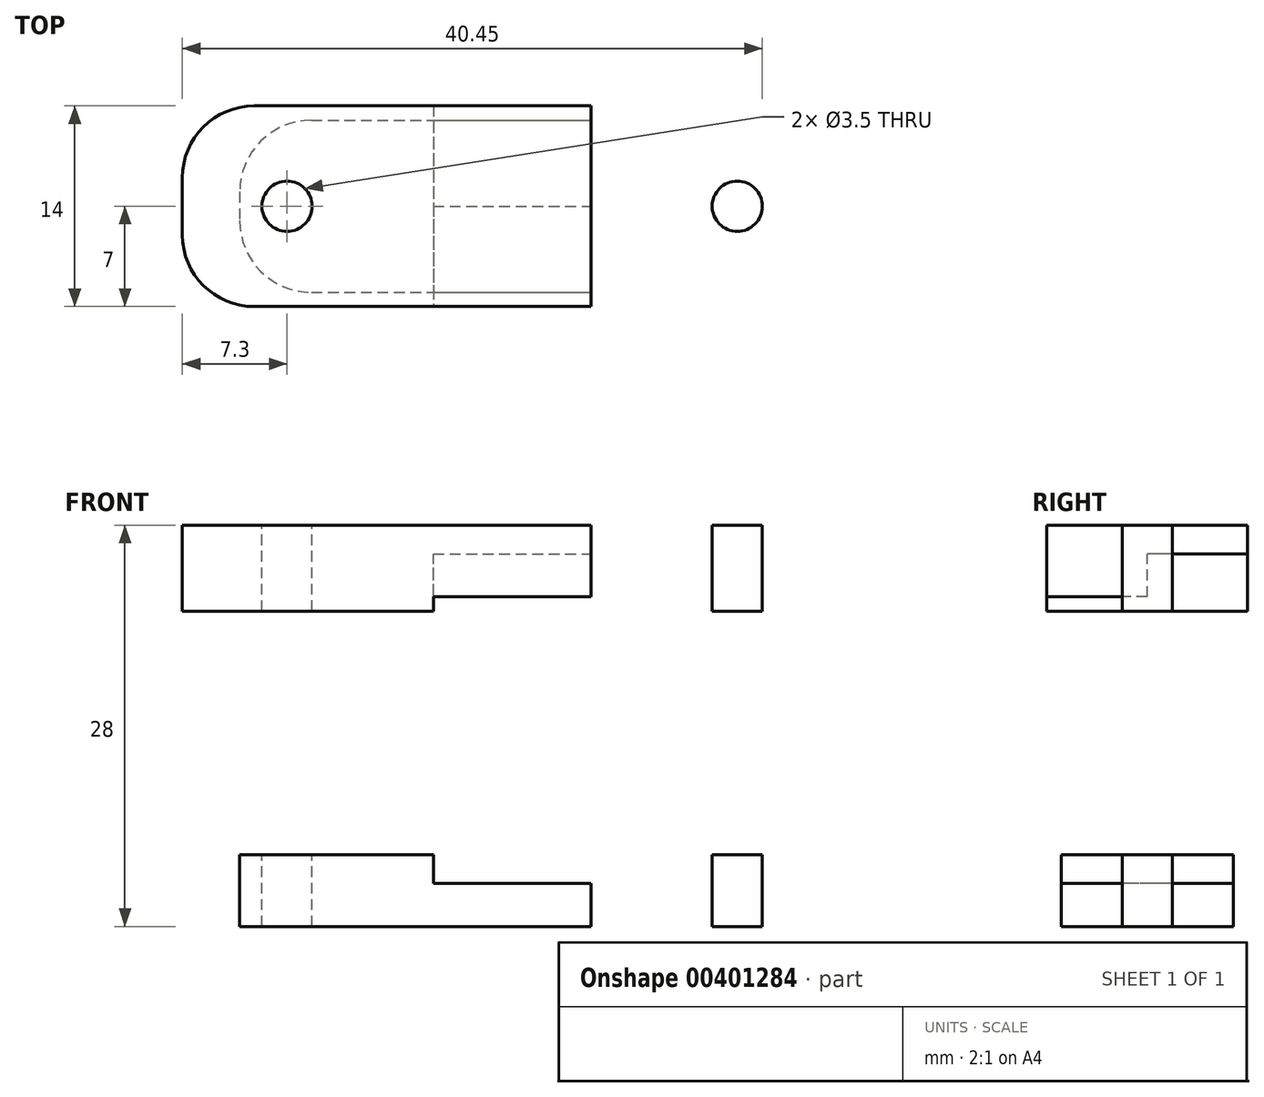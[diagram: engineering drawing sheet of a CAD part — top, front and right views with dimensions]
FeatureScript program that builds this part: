
annotation { "Feature Type Name" : "Feature", "Feature Type Description" : "" }
export const myFeature = defineFeature(function(context is Context, id is Id, definition is map)
    precondition{}
    {
        {
            var Q0;
            Q0=qCreatedBy(makeId("Top.planeOp"),FACE);
            var sketch = newSketch(context, id + "F0", { "sketchPlane" : qUnion([Q0])});
            skCircle(sketch, "E0", {"center": v(-15.7, 0) * mm, "radius": 1.75 * mm});
            skCircle(sketch, "E1.MirrorC", {"center": v(15.7, 0) * mm, "radius": 1.75 * mm});
            skLineSegment(sketch, "E2.bottom", {"start": v(-19, 6) * mm, "end": v(19, 6) * mm});
            skLineSegment(sketch, "E2.top", {"start": v(-19, -6) * mm, "end": v(19, -6) * mm});
            skLineSegment(sketch, "E2.left", {"start": v(-19, 6) * mm, "end": v(-19, -6) * mm});
            skLineSegment(sketch, "E2.right", {"start": v(19, 6) * mm, "end": v(19, -6) * mm});
            skPoint(sketch, "E2.middle", {"position": v(0, 0) * mm});
            skLineSegment(sketch, "E3", {"start": v(-5.5, 6) * mm, "end": v(-5.5, -6) * mm});
            skLineSegment(sketch, "E4.MirrorCS", {"start": v(5.5, 6) * mm, "end": v(5.5, -6) * mm});
            skSolve(sketch);
        }
        {
            var Q0;
            Q0=makeQuery(id+"F0.imprint","IMPRINT",FACE,{"disambiguationData":[TD([[makeQuery(id+"F0.imprint","IMPRINT",EDGE,{"derivedFrom":sQuery(id+"F0.wireOp",EDGE,"E0")}),-1.0]])]});
            var Q1;
            {var subQ0=sQuery(id+"F0.wireOp",EDGE,"E3");Q1=makeQuery(id+"F0.imprint","IMPRINT",FACE,{"disambiguationData":[TD([[makeQuery(id+"F0.imprint","IMPRINT",EDGE,{"derivedFrom":subQ0}),1.0]])]});}
            var Q2;
            Q2=makeQuery(id+"F0.imprint","IMPRINT",FACE,{"disambiguationData":[TD([[makeQuery(id+"F0.imprint","IMPRINT",EDGE,{"derivedFrom":sQuery(id+"F0.wireOp",EDGE,"E1.MirrorC")}),1.0]])]});
            extrude(context, id + "F1", {"entities" : qUnion([Q0, Q1, Q2]), "oppositeDirection" : true, "depth" : 3 * mm});
        }
        {
            var Q0;
            Q0=makeQuery(id+"F0.imprint","IMPRINT",FACE,{"disambiguationData":[TD([[makeQuery(id+"F0.imprint","IMPRINT",EDGE,{"derivedFrom":sQuery(id+"F0.wireOp",EDGE,"E0")}),-1.0]])]});
            var Q1;
            Q1=makeQuery(id+"F0.imprint","IMPRINT",FACE,{"disambiguationData":[TD([[makeQuery(id+"F0.imprint","IMPRINT",EDGE,{"derivedFrom":sQuery(id+"F0.wireOp",EDGE,"E1.MirrorC")}),1.0]])]});
            extrude(context, id + "F2", {"entities" : qUnion([Q0, Q1]), "operationType" : NewBodyOperationType.ADD, "depth" : 2 * mm});
        }
        {
            var Q0;
            Q0=qCreatedBy(makeId("Top.planeOp"),FACE);
            cPlane(context, id + "F3", {"entities" : qUnion([Q0]), "cplaneType" : CPlaneType.OFFSET, "offset" : 25 * mm, "width" : 150 * mm, "height" : 150 * mm});
        }
        {
            var Q0;
            Q0=qCreatedBy(id+"F3.planeOp",FACE);
            var sketch = newSketch(context, id + "F4", { "sketchPlane" : qUnion([Q0])});
            skCircle(sketch, "E5", {"center": v(-15.7, 0) * mm, "radius": 1.75 * mm});
            skCircle(sketch, "E6.MirrorC", {"center": v(15.7, 0) * mm, "radius": 1.75 * mm});
            skLineSegment(sketch, "E7.bottom", {"start": v(-23, 7) * mm, "end": v(23, 7) * mm});
            skLineSegment(sketch, "E7.top", {"start": v(-23, -7) * mm, "end": v(23, -7) * mm});
            skLineSegment(sketch, "E7.left", {"start": v(-23, 7) * mm, "end": v(-23, -7) * mm});
            skLineSegment(sketch, "E7.right", {"start": v(23, 7) * mm, "end": v(23, -7) * mm});
            skPoint(sketch, "E7.middle", {"position": v(0, 0) * mm});
            skLineSegment(sketch, "E8", {"start": v(-5.5, 7) * mm, "end": v(-5.5, -7) * mm});
            skLineSegment(sketch, "E9.MirrorCS", {"start": v(5.5, 7) * mm, "end": v(5.5, -7) * mm});
            skLineSegment(sketch, "E10", {"start": v(-5.5, 0) * mm, "end": v(5.5, 0) * mm});
            skSolve(sketch);
        }
        {
            var Q0;
            Q0=makeQuery(id+"F4.imprint","IMPRINT",FACE,{"disambiguationData":[TD([[makeQuery(id+"F4.imprint","IMPRINT",EDGE,{"derivedFrom":sQuery(id+"F4.wireOp",EDGE,"E5")}),-1.0]])]});
            var Q1;
            {var subQ5=sQuery(id+"F4.wireOp",EDGE,"E10");Q1=makeQuery(id+"F4.imprint","IMPRINT",FACE,{"disambiguationData":[TD([[makeQuery(id+"F4.imprint","IMPRINT",EDGE,{"derivedFrom":subQ5}),1.0]])]});}
            var Q2;
            {var subQ5=sQuery(id+"F4.wireOp",EDGE,"E10");Q2=makeQuery(id+"F4.imprint","IMPRINT",FACE,{"disambiguationData":[TD([[makeQuery(id+"F4.imprint","IMPRINT",EDGE,{"derivedFrom":subQ5}),-1.0]])]});}
            var Q3;
            Q3=makeQuery(id+"F4.imprint","IMPRINT",FACE,{"disambiguationData":[TD([[makeQuery(id+"F4.imprint","IMPRINT",EDGE,{"derivedFrom":sQuery(id+"F4.wireOp",EDGE,"E6.MirrorC")}),1.0]])]});
            extrude(context, id + "F5", {"entities" : qUnion([Q0, Q1, Q2, Q3]), "oppositeDirection" : true, "depth" : 2 * mm});
        }
        {
            var Q0;
            Q0=makeQuery(id+"F4.imprint","IMPRINT",FACE,{"disambiguationData":[TD([[makeQuery(id+"F4.imprint","IMPRINT",EDGE,{"derivedFrom":sQuery(id+"F4.wireOp",EDGE,"E5")}),-1.0]])]});
            var Q1;
            Q1=makeQuery(id+"F4.imprint","IMPRINT",FACE,{"disambiguationData":[TD([[makeQuery(id+"F4.imprint","IMPRINT",EDGE,{"derivedFrom":sQuery(id+"F4.wireOp",EDGE,"E6.MirrorC")}),1.0]])]});
            extrude(context, id + "F6", {"entities" : qUnion([Q0, Q1]), "operationType" : NewBodyOperationType.ADD, "oppositeDirection" : true, "depth" : 6 * mm});
        }
        {
            var Q0;
            {var subQ5=sQuery(id+"F4.wireOp",EDGE,"E10");Q0=makeQuery(id+"F4.imprint","IMPRINT",FACE,{"disambiguationData":[TD([[makeQuery(id+"F4.imprint","IMPRINT",EDGE,{"derivedFrom":subQ5}),-1.0]])]});}
            extrude(context, id + "F7", {"entities" : qUnion([Q0]), "operationType" : NewBodyOperationType.ADD, "oppositeDirection" : true, "depth" : 5 * mm});
        }
        {
            var Q0;
            {var subQ0=sQuery(id+"F0.wireOp",EDGE,"E2.left");var subQ1=sQuery(id+"F0.wireOp",EDGE,"E2.top");Q0=makeQuery(id+"F2.boolean.opBoolean","MERGE",EDGE,{"derivedFrom":[makeQuery(id+"F1.opExtrude","SWEPT_EDGE",EDGE,{"disambiguationData":[OSD([subQ1,subQ0])]}),makeQuery(id+"F2.opExtrude","SWEPT_EDGE",EDGE,{"disambiguationData":[OSD([subQ1,subQ0])]})]});}
            var Q1;
            {var subQ0=sQuery(id+"F0.wireOp",EDGE,"E2.left");var subQ1=sQuery(id+"F0.wireOp",EDGE,"E2.bottom");Q1=makeQuery(id+"F2.boolean.opBoolean","MERGE",EDGE,{"derivedFrom":[makeQuery(id+"F1.opExtrude","SWEPT_EDGE",EDGE,{"disambiguationData":[OSD([subQ1,subQ0])]}),makeQuery(id+"F2.opExtrude","SWEPT_EDGE",EDGE,{"disambiguationData":[OSD([subQ1,subQ0])]})]});}
            var Q2;
            {var subQ0=sQuery(id+"F0.wireOp",EDGE,"E2.right");var subQ1=sQuery(id+"F0.wireOp",EDGE,"E2.top");Q2=makeQuery(id+"F2.boolean.opBoolean","MERGE",EDGE,{"derivedFrom":[makeQuery(id+"F1.opExtrude","SWEPT_EDGE",EDGE,{"disambiguationData":[OSD([subQ1,subQ0])]}),makeQuery(id+"F2.opExtrude","SWEPT_EDGE",EDGE,{"disambiguationData":[OSD([subQ1,subQ0])]})]});}
            var Q3;
            {var subQ0=sQuery(id+"F0.wireOp",EDGE,"E2.right");var subQ1=sQuery(id+"F0.wireOp",EDGE,"E2.bottom");Q3=makeQuery(id+"F2.boolean.opBoolean","MERGE",EDGE,{"derivedFrom":[makeQuery(id+"F1.opExtrude","SWEPT_EDGE",EDGE,{"disambiguationData":[OSD([subQ1,subQ0])]}),makeQuery(id+"F2.opExtrude","SWEPT_EDGE",EDGE,{"disambiguationData":[OSD([subQ1,subQ0])]})]});}
            var Q4;
            {var subQ0=sQuery(id+"F4.wireOp",EDGE,"E7.left");var subQ1=sQuery(id+"F4.wireOp",EDGE,"E7.bottom");Q4=makeQuery(id+"F6.boolean.opBoolean","MERGE",EDGE,{"derivedFrom":[makeQuery(id+"F5.opExtrude","SWEPT_EDGE",EDGE,{"disambiguationData":[OSD([subQ1,subQ0])]}),makeQuery(id+"F6.opExtrude","SWEPT_EDGE",EDGE,{"disambiguationData":[OSD([subQ1,subQ0])]})]});}
            var Q5;
            {var subQ0=sQuery(id+"F4.wireOp",EDGE,"E7.left");var subQ1=sQuery(id+"F4.wireOp",EDGE,"E7.top");Q5=makeQuery(id+"F6.boolean.opBoolean","MERGE",EDGE,{"derivedFrom":[makeQuery(id+"F5.opExtrude","SWEPT_EDGE",EDGE,{"disambiguationData":[OSD([subQ1,subQ0])]}),makeQuery(id+"F6.opExtrude","SWEPT_EDGE",EDGE,{"disambiguationData":[OSD([subQ1,subQ0])]})]});}
            var Q6;
            {var subQ0=sQuery(id+"F4.wireOp",EDGE,"E7.right");var subQ1=sQuery(id+"F4.wireOp",EDGE,"E7.bottom");Q6=makeQuery(id+"F6.boolean.opBoolean","MERGE",EDGE,{"derivedFrom":[makeQuery(id+"F5.opExtrude","SWEPT_EDGE",EDGE,{"disambiguationData":[OSD([subQ1,subQ0])]}),makeQuery(id+"F6.opExtrude","SWEPT_EDGE",EDGE,{"disambiguationData":[OSD([subQ1,subQ0])]})]});}
            var Q7;
            {var subQ0=sQuery(id+"F4.wireOp",EDGE,"E7.right");var subQ1=sQuery(id+"F4.wireOp",EDGE,"E7.top");Q7=makeQuery(id+"F6.boolean.opBoolean","MERGE",EDGE,{"derivedFrom":[makeQuery(id+"F5.opExtrude","SWEPT_EDGE",EDGE,{"disambiguationData":[OSD([subQ1,subQ0])]}),makeQuery(id+"F6.opExtrude","SWEPT_EDGE",EDGE,{"disambiguationData":[OSD([subQ1,subQ0])]})]});}
            fillet(context, id + "F8", {"entities" : qUnion([Q0, Q1, Q2, Q3, Q4, Q5, Q6, Q7]), "radius" : 5 * mm, "tangentPropagation" : true, "allowEdgeOverflow" : false});
        }
    });
